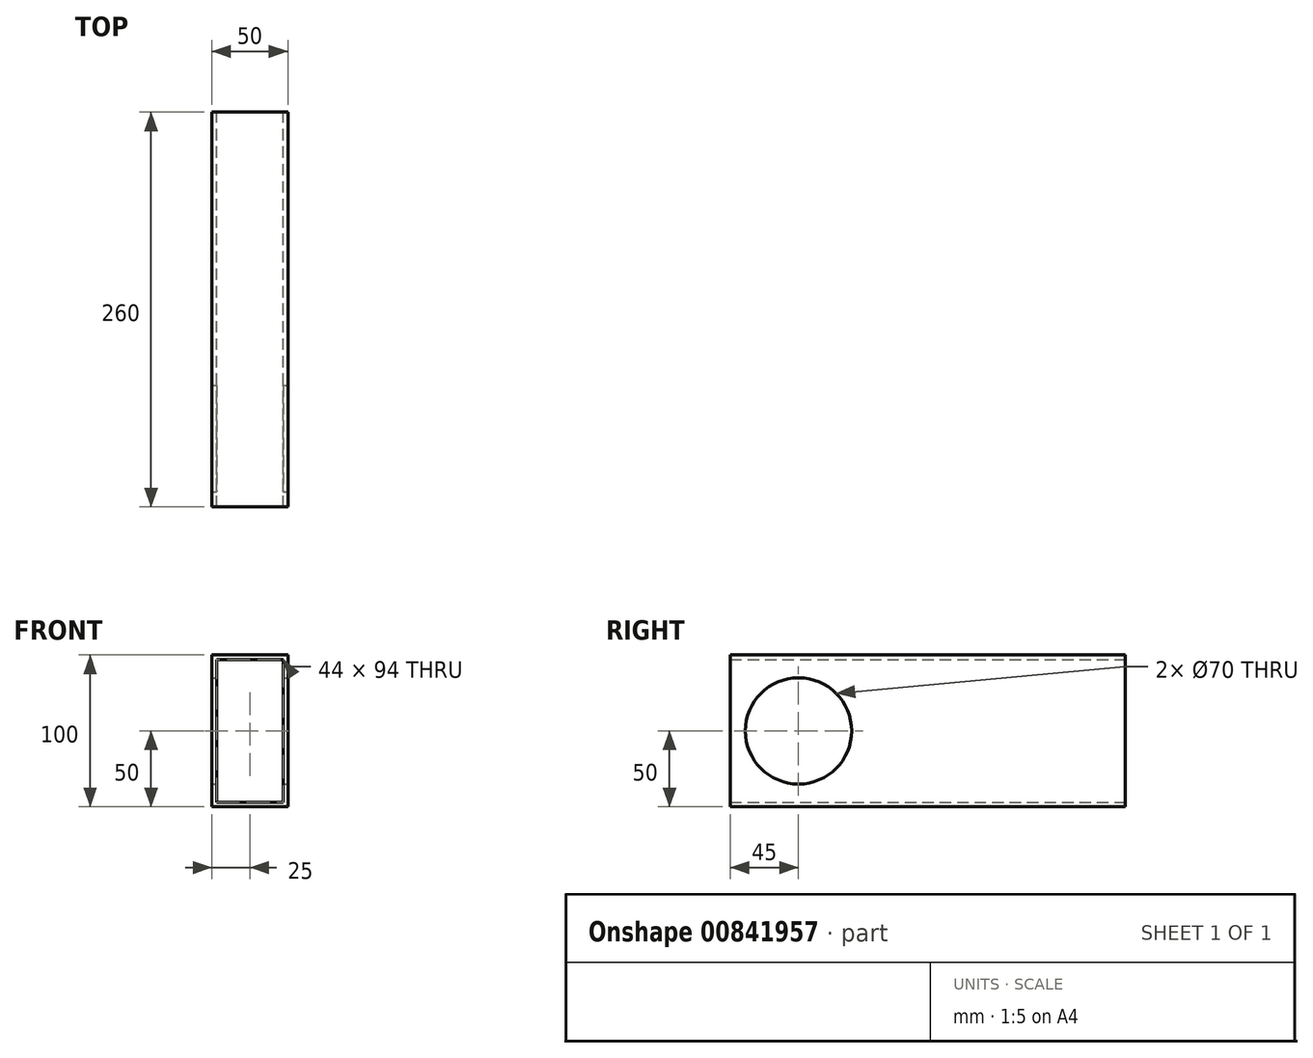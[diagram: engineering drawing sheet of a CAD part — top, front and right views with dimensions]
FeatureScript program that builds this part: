
annotation { "Feature Type Name" : "Feature", "Feature Type Description" : "" }
export const myFeature = defineFeature(function(context is Context, id is Id, definition is map)
    precondition{}
    {
        {
            var Q0;
            Q0=qCreatedBy(makeId("Front.planeOp"),FACE);
            var sketch = newSketch(context, id + "F0", { "sketchPlane" : qUnion([Q0])});
            skLineSegment(sketch, "E0.bottom", {"start": v(-25, 50) * mm, "end": v(25, 50) * mm});
            skLineSegment(sketch, "E0.top", {"start": v(-25, -50) * mm, "end": v(25, -50) * mm});
            skLineSegment(sketch, "E0.left", {"start": v(-25, 50) * mm, "end": v(-25, -50) * mm});
            skLineSegment(sketch, "E0.right", {"start": v(25, 50) * mm, "end": v(25, -50) * mm});
            skLineSegment(sketch, "E1.0", {"start": v(-22, 47) * mm, "end": v(-22, -47) * mm});
            skLineSegment(sketch, "E1.1", {"start": v(-22, 47) * mm, "end": v(22, 47) * mm});
            skLineSegment(sketch, "E1.2", {"start": v(22, 47) * mm, "end": v(22, -47) * mm});
            skLineSegment(sketch, "E1.3", {"start": v(-22, -47) * mm, "end": v(22, -47) * mm});
            skSolve(sketch);
        }
        {
            var Q0;
            Q0=makeQuery(id+"F0.imprint","IMPRINT",FACE,{"disambiguationData":[TD([[makeQuery(id+"F0.imprint","IMPRINT",EDGE,{"derivedFrom":sQuery(id+"F0.wireOp",EDGE,"E0.bottom")}),-1.0]])]});
            extrude(context, id + "F1", {"entities" : qUnion([Q0]), "endBound" : BoundingType.SYMMETRIC, "depth" : 260 * mm, "offsetDistance" : 25 * mm});
        }
        {
            var Q0;
            Q0=makeQuery(id+"F1.opExtrude","SWEPT_FACE",FACE,{"disambiguationData":[OSD([sQuery(id+"F0.wireOp",EDGE,"E0.right")])]});
            var sketch = newSketch(context, id + "F2", { "sketchPlane" : qUnion([Q0])});
            skCircle(sketch, "E2", {"center": v(-85, 0) * mm, "radius": 35 * mm});
            skPoint(sketch, "E2.centerSnap0", {"position": v(-130, 0) * mm});
            skSolve(sketch);
        }
        {
            var Q0;
            Q0=sQuery(id+"F2.wireOp",VERTEX,"E2.center");
            var Q1;
            Q1=makeQuery(id+"F1.opExtrude","SWEPT_BODY",BODY,{"disambiguationData":[OSD([sQuery(id+"F0.wireOp",EDGE,"E0.bottom"),sQuery(id+"F0.wireOp",EDGE,"E0.top"),sQuery(id+"F0.wireOp",EDGE,"E0.left"),sQuery(id+"F0.wireOp",EDGE,"E0.right"),sQuery(id+"F0.wireOp",EDGE,"E1.0"),sQuery(id+"F0.wireOp",EDGE,"E1.1"),sQuery(id+"F0.wireOp",EDGE,"E1.2"),sQuery(id+"F0.wireOp",EDGE,"E1.3")])]});
            hole(context, id + "F3", {"style" : HoleStyle.SIMPLE, "endStyle" : HoleEndStyle.THROUGH, "holeDiameter" : 70 * mm, "majorDiameter" : 5 * mm, "isTappedThrough" : true, "tappedDepth" : 12 * mm, "tapClearance" : 3, "locations" : qUnion([Q0]), "scope" : qUnion([Q1])});
        }
    });
